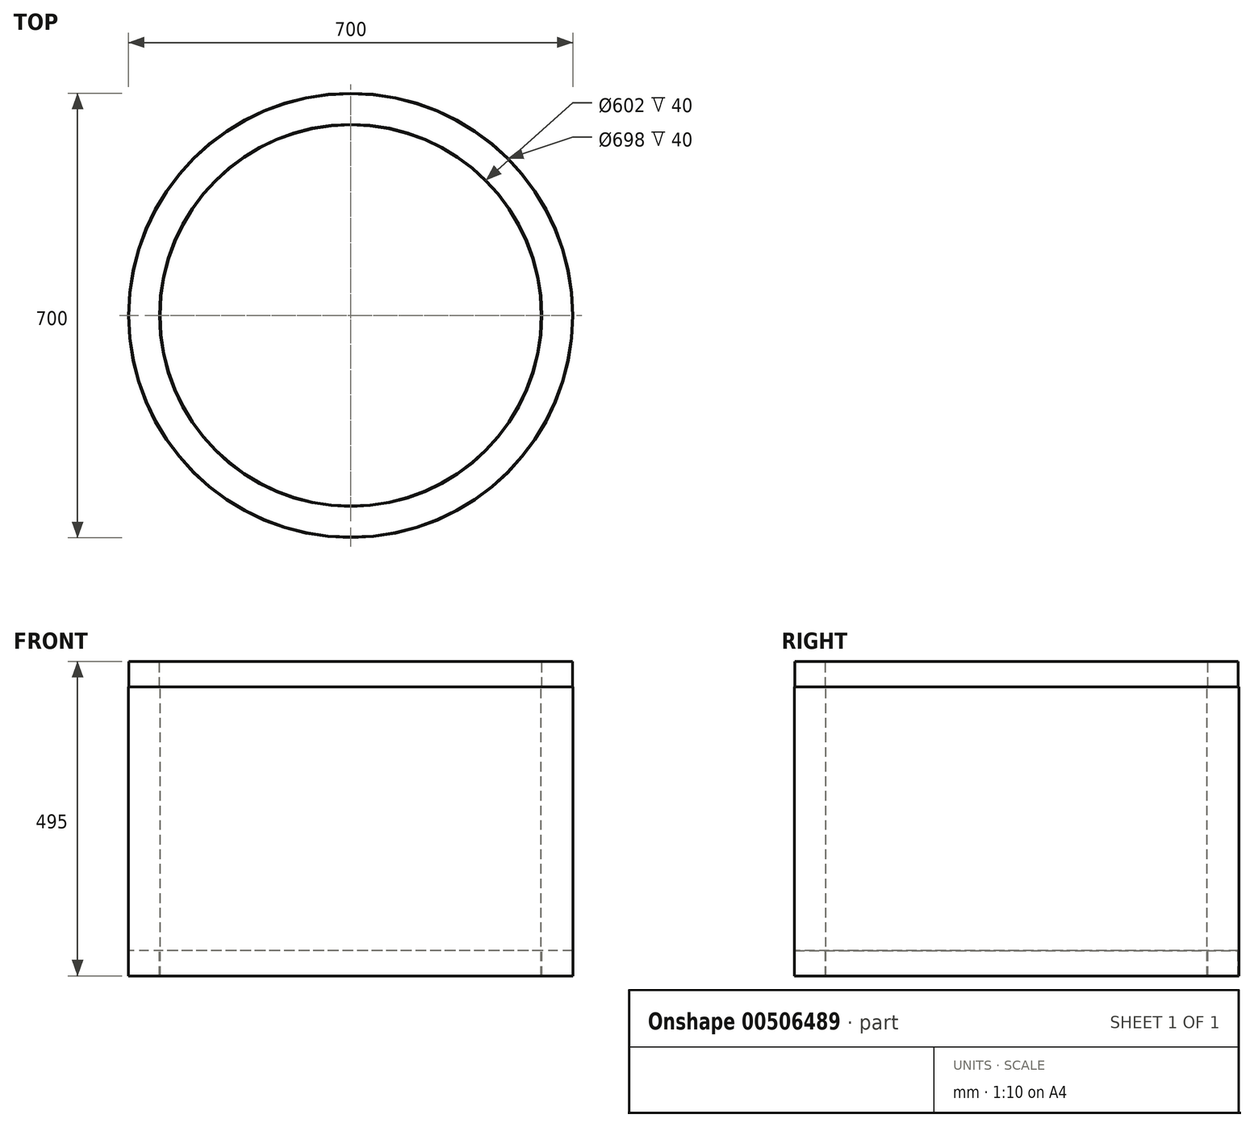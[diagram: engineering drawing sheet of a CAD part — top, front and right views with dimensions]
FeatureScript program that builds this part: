
annotation { "Feature Type Name" : "Feature", "Feature Type Description" : "" }
export const myFeature = defineFeature(function(context is Context, id is Id, definition is map)
    precondition{}
    {
        {
            var Q0;
            Q0=qCreatedBy(makeId("Front.planeOp"),FACE);
            var sketch = newSketch(context, id + "F0", { "sketchPlane" : qUnion([Q0])});
            skLineSegment(sketch, "E0", {"start": v(0, 74.87) * mm, "end": v(0, -73.71) * mm, "construction": true});
            skLineSegment(sketch, "E1", {"start": v(0, 374.84) * mm, "end": v(0, -528.94) * mm, "construction": true});
            skLineSegment(sketch, "E2", {"start": v(-300, -489.75) * mm, "end": v(-300, -34.75) * mm});
            skLineSegment(sketch, "E3", {"start": v(-300, -34.75) * mm, "end": v(-301, -34.75) * mm});
            skLineSegment(sketch, "E4", {"start": v(-301, -34.75) * mm, "end": v(-301, 5.25) * mm});
            skLineSegment(sketch, "E5", {"start": v(-301, 5.25) * mm, "end": v(-349, 5.25) * mm});
            skLineSegment(sketch, "E6", {"start": v(-349, 5.25) * mm, "end": v(-349, -34.75) * mm});
            skLineSegment(sketch, "E7", {"start": v(-349, -34.75) * mm, "end": v(-350, -34.75) * mm});
            skLineSegment(sketch, "E8", {"start": v(-350, -34.75) * mm, "end": v(-350, -489.75) * mm});
            skLineSegment(sketch, "E9", {"start": v(-350, -489.75) * mm, "end": v(-349, -489.75) * mm});
            skLineSegment(sketch, "E10", {"start": v(-349, -489.75) * mm, "end": v(-349, -449.75) * mm});
            skLineSegment(sketch, "E11", {"start": v(-349, -449.75) * mm, "end": v(-301, -449.75) * mm});
            skLineSegment(sketch, "E12", {"start": v(-301, -449.75) * mm, "end": v(-301, -489.75) * mm});
            skLineSegment(sketch, "E13", {"start": v(-301, -489.75) * mm, "end": v(-300, -489.75) * mm});
            skSolve(sketch);
        }
        {
            var Q0;
            Q0=qSketchRegion(id+"F0",true);
            var Q1;
            Q1=sQuery(id+"F0.wireOp",EDGE,"E1");
            revolve(context, id + "F1", {"entities" : qUnion([Q0]), "axis" : qUnion([Q1]), "revolveType" : RevolveType.FULL});
        }
    });
